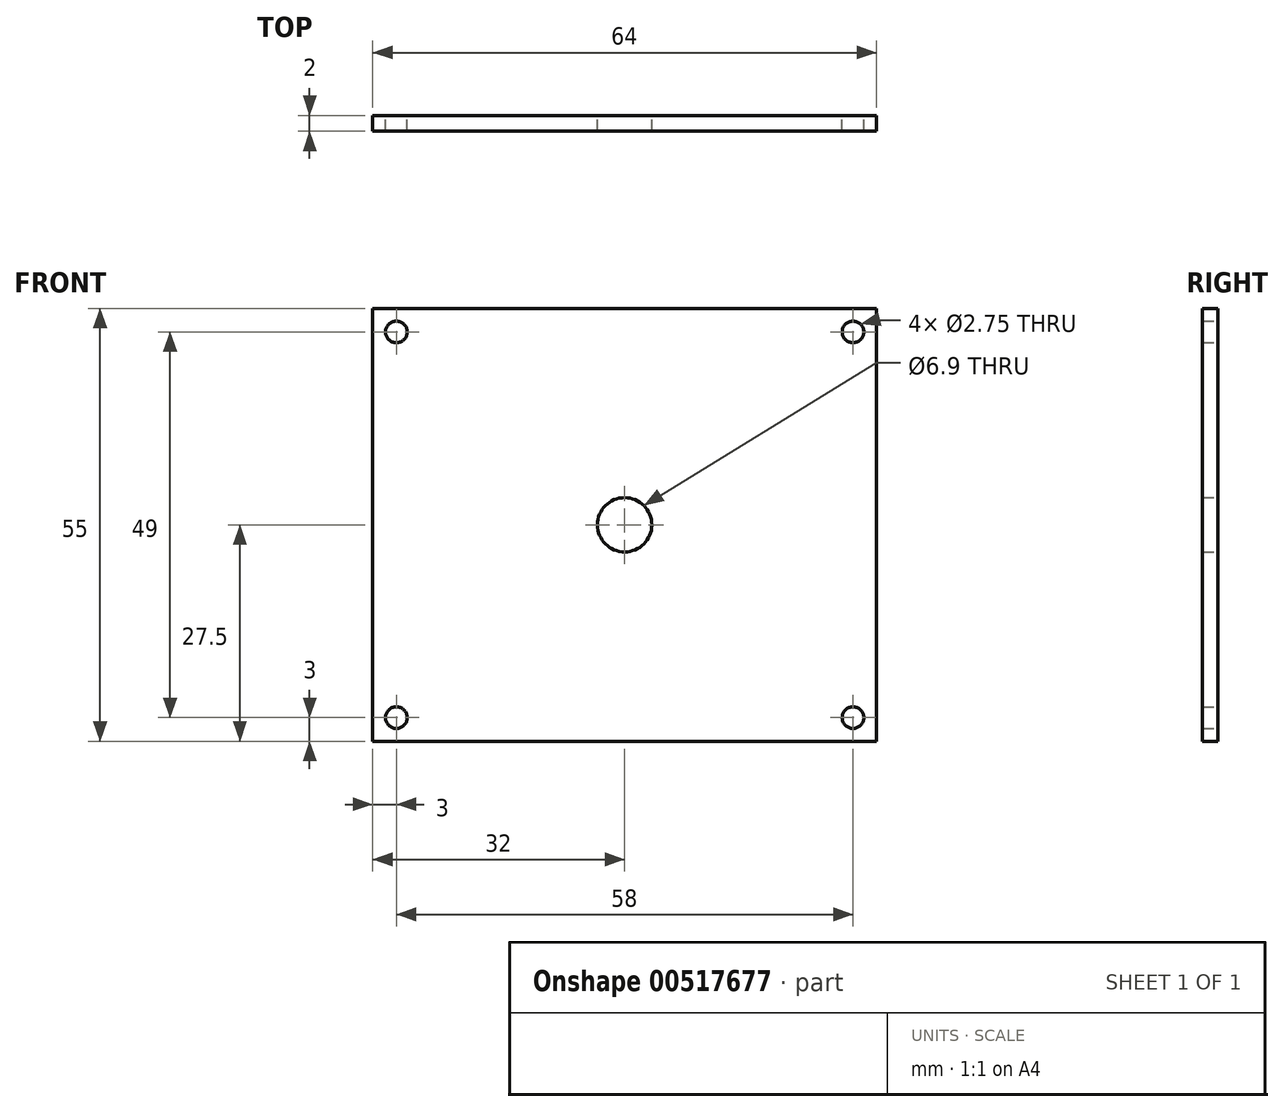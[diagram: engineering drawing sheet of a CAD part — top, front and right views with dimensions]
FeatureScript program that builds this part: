
annotation { "Feature Type Name" : "Feature", "Feature Type Description" : "" }
export const myFeature = defineFeature(function(context is Context, id is Id, definition is map)
    precondition{}
    {
        {
            var Q0;
            Q0=qCreatedBy(makeId("Front.planeOp"),FACE);
            var sketch = newSketch(context, id + "F0", { "sketchPlane" : qUnion([Q0])});
            skLineSegment(sketch, "E0.bottom", {"start": v(-32, 27.5) * mm, "end": v(32, 27.5) * mm});
            skLineSegment(sketch, "E0.top", {"start": v(-32, -27.5) * mm, "end": v(32, -27.5) * mm});
            skLineSegment(sketch, "E0.left", {"start": v(-32, 27.5) * mm, "end": v(-32, -27.5) * mm});
            skLineSegment(sketch, "E0.right", {"start": v(32, 27.5) * mm, "end": v(32, -27.5) * mm});
            skPoint(sketch, "E1", {"position": v(-32, 0) * mm});
            skPoint(sketch, "E2", {"position": v(0, 27.5) * mm});
            skCircle(sketch, "E3", {"center": v(-29, 24.5) * mm, "radius": 1.38 * mm});
            skCircle(sketch, "E4", {"center": v(29, 24.5) * mm, "radius": 1.38 * mm});
            skCircle(sketch, "E5", {"center": v(-29, -24.5) * mm, "radius": 1.38 * mm});
            skCircle(sketch, "E6", {"center": v(29, -24.5) * mm, "radius": 1.38 * mm});
            skCircle(sketch, "E7", {"center": v(0, 0) * mm, "radius": 3.45 * mm});
            skSolve(sketch);
        }
        {
            var Q0;
            Q0 = qSketchRegion(id + "F0", true);
            extrude(context, id + "F1", {"entities" : qUnion([Q0]), "depth" : 2 * mm, "offsetDistance" : 25 * mm});
        }
    });
